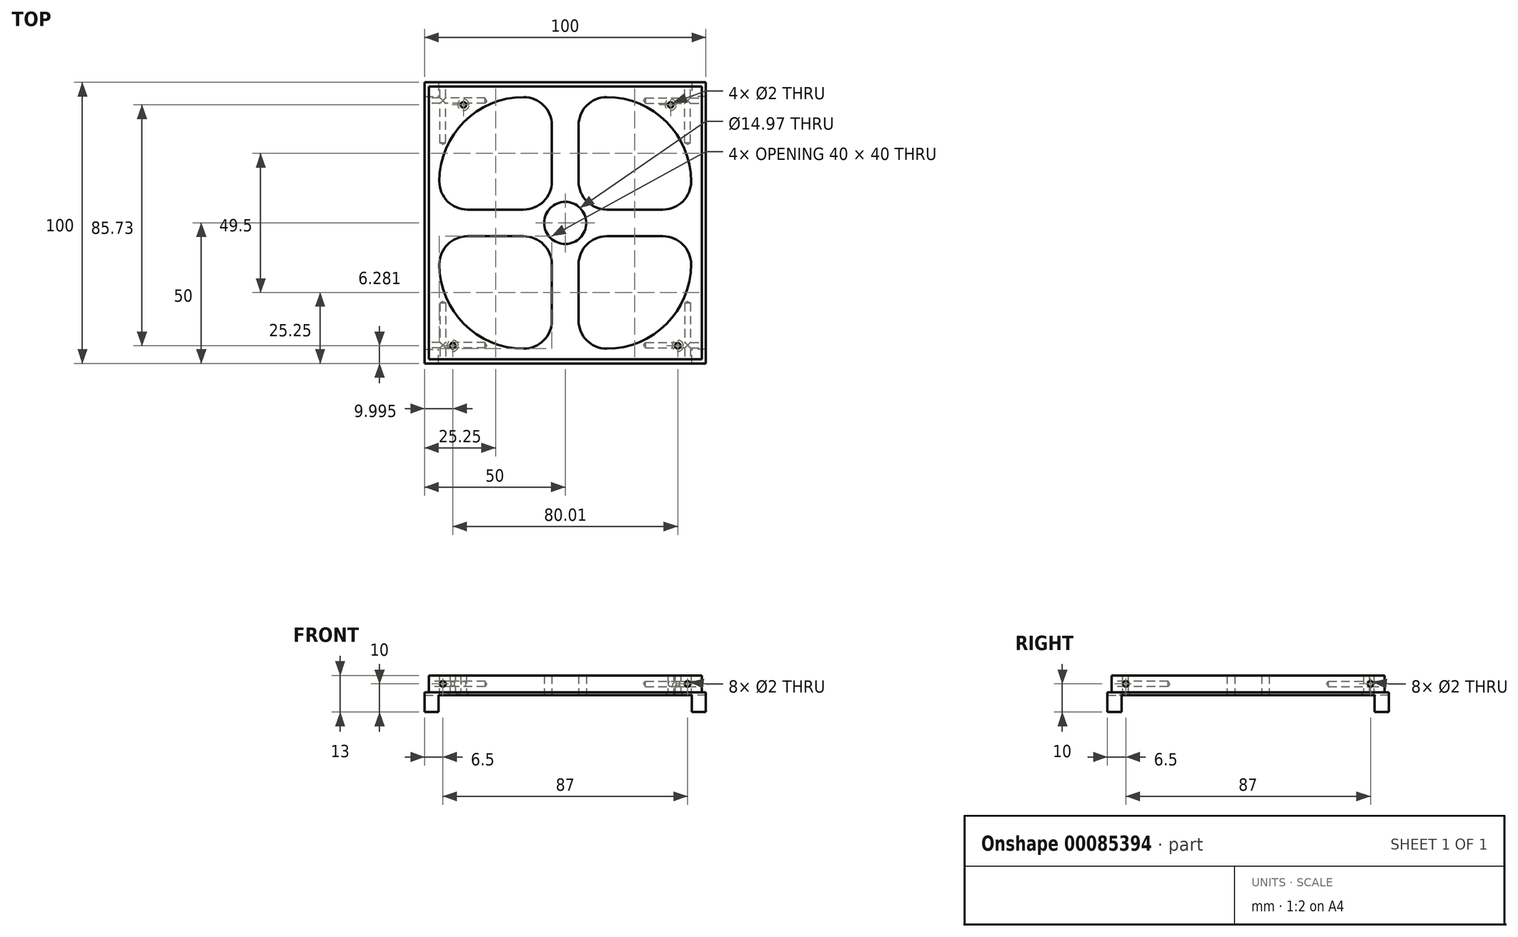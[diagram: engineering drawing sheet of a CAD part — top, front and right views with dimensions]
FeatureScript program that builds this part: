
annotation { "Feature Type Name" : "Feature", "Feature Type Description" : "" }
export const myFeature = defineFeature(function(context is Context, id is Id, definition is map)
    precondition{}
    {
        {
            var Q0;
            Q0=qCreatedBy(makeId("Top.planeOp"),FACE);
            var sketch = newSketch(context, id + "F0", { "sketchPlane" : qUnion([Q0])});
            skLineSegment(sketch, "E0.rect.bottom", {"start": v(-50, 50) * mm, "end": v(50, 50) * mm});
            skLineSegment(sketch, "E0.rect.top", {"start": v(-50, -50) * mm, "end": v(50, -50) * mm});
            skLineSegment(sketch, "E0.rect.left", {"start": v(-50, 50) * mm, "end": v(-50, -50) * mm});
            skLineSegment(sketch, "E0.rect.right", {"start": v(50, 50) * mm, "end": v(50, -50) * mm});
            skPoint(sketch, "E0.rect.middle", {"position": v(0, 0) * mm});
            skLineSegment(sketch, "E1.rect.bottom", {"start": v(-48.5, 48.5) * mm, "end": v(48.5, 48.5) * mm});
            skLineSegment(sketch, "E1.rect.top", {"start": v(-48.5, -48.5) * mm, "end": v(48.5, -48.5) * mm});
            skLineSegment(sketch, "E1.rect.left", {"start": v(-48.5, 48.5) * mm, "end": v(-48.5, -48.5) * mm});
            skLineSegment(sketch, "E1.rect.right", {"start": v(48.5, 48.5) * mm, "end": v(48.5, -48.5) * mm});
            skLineSegment(sketch, "E2.rect.bottom", {"start": v(-14.75, 4.75) * mm, "end": v(-34.75, 4.75) * mm});
            skLineSegment(sketch, "E2.rect.top", {"start": v(-14.75, 44.75) * mm, "end": v(-14.75, 44.75) * mm});
            skLineSegment(sketch, "E2.rect.left", {"start": v(-4.75, 14.75) * mm, "end": v(-4.75, 34.75) * mm});
            skLineSegment(sketch, "E2.rect.right", {"start": v(-44.75, 14.75) * mm, "end": v(-44.75, 14.75) * mm});
            skPoint(sketch, "E2.rect.middle", {"position": v(-24.75, 24.75) * mm});
            skPoint(sketch, "E3.visualSharp", {"position": v(-44.75, 44.75) * mm});
            skArc(sketch, "E3.filletArc", {"start": v(-14.75, 44.75) * mm, "mid": v(-35.96, 35.96) * mm, "end": v(-44.75, 14.75) * mm});
            skPoint(sketch, "E4.visualSharp", {"position": v(-4.75, 44.75) * mm});
            skArc(sketch, "E4.filletArc", {"start": v(-4.75, 34.75) * mm, "mid": v(-7.68, 41.82) * mm, "end": v(-14.75, 44.75) * mm});
            skPoint(sketch, "E5.visualSharp", {"position": v(-4.75, 4.75) * mm});
            skArc(sketch, "E5.filletArc", {"start": v(-14.75, 4.75) * mm, "mid": v(-7.68, 7.68) * mm, "end": v(-4.75, 14.75) * mm});
            skPoint(sketch, "E6.visualSharp", {"position": v(-44.75, 4.75) * mm});
            skArc(sketch, "E6.filletArc", {"start": v(-44.75, 14.75) * mm, "mid": v(-41.82, 7.68) * mm, "end": v(-34.75, 4.75) * mm});
            skLineSegment(sketch, "E7.MirrorCS", {"start": v(4.75, 14.75) * mm, "end": v(4.75, 34.75) * mm});
            skArc(sketch, "E8.MirrorCS", {"start": v(4.75, 34.75) * mm, "mid": v(7.68, 41.82) * mm, "end": v(14.75, 44.75) * mm});
            skLineSegment(sketch, "E9.MirrorCS", {"start": v(14.75, 44.75) * mm, "end": v(14.75, 44.75) * mm});
            skArc(sketch, "E10.MirrorCS", {"start": v(14.75, 44.75) * mm, "mid": v(35.96, 35.96) * mm, "end": v(44.75, 14.75) * mm});
            skLineSegment(sketch, "E11.MirrorCS", {"start": v(44.75, 14.75) * mm, "end": v(44.75, 14.75) * mm});
            skArc(sketch, "E12.MirrorCS", {"start": v(44.75, 14.75) * mm, "mid": v(41.82, 7.68) * mm, "end": v(34.75, 4.75) * mm});
            skLineSegment(sketch, "E13.MirrorCS", {"start": v(14.75, 4.75) * mm, "end": v(34.75, 4.75) * mm});
            skArc(sketch, "E14.MirrorCS", {"start": v(14.75, 4.75) * mm, "mid": v(7.68, 7.68) * mm, "end": v(4.75, 14.75) * mm});
            skPoint(sketch, "E15.MirrorP", {"position": v(24.75, 24.75) * mm});
            skArc(sketch, "E16.MirrorCS", {"start": v(14.75, -4.75) * mm, "mid": v(7.68, -7.68) * mm, "end": v(4.75, -14.75) * mm});
            skLineSegment(sketch, "E17.MirrorCS", {"start": v(4.75, -14.75) * mm, "end": v(4.75, -34.75) * mm});
            skArc(sketch, "E18.MirrorCS", {"start": v(4.75, -34.75) * mm, "mid": v(7.68, -41.82) * mm, "end": v(14.75, -44.75) * mm});
            skLineSegment(sketch, "E19.MirrorCS", {"start": v(14.75, -44.75) * mm, "end": v(14.75, -44.75) * mm});
            skArc(sketch, "E20.MirrorCS", {"start": v(14.75, -44.75) * mm, "mid": v(35.96, -35.96) * mm, "end": v(44.75, -14.75) * mm});
            skLineSegment(sketch, "E21.MirrorCS", {"start": v(44.75, -14.75) * mm, "end": v(44.75, -14.75) * mm});
            skArc(sketch, "E22.MirrorCS", {"start": v(44.75, -14.75) * mm, "mid": v(41.82, -7.68) * mm, "end": v(34.75, -4.75) * mm});
            skLineSegment(sketch, "E23.MirrorCS", {"start": v(14.75, -4.75) * mm, "end": v(34.75, -4.75) * mm});
            skPoint(sketch, "E24.MirrorP", {"position": v(24.75, -24.75) * mm});
            skLineSegment(sketch, "E25.MirrorCS", {"start": v(-4.75, -14.75) * mm, "end": v(-4.75, -34.75) * mm});
            skArc(sketch, "E26.MirrorCS", {"start": v(-14.75, -4.75) * mm, "mid": v(-7.68, -7.68) * mm, "end": v(-4.75, -14.75) * mm});
            skLineSegment(sketch, "E27.MirrorCS", {"start": v(-14.75, -4.75) * mm, "end": v(-34.75, -4.75) * mm});
            skArc(sketch, "E28.MirrorCS", {"start": v(-44.75, -14.75) * mm, "mid": v(-41.82, -7.68) * mm, "end": v(-34.75, -4.75) * mm});
            skLineSegment(sketch, "E29.MirrorCS", {"start": v(-44.75, -14.75) * mm, "end": v(-44.75, -14.75) * mm});
            skArc(sketch, "E30.MirrorCS", {"start": v(-14.75, -44.75) * mm, "mid": v(-35.96, -35.96) * mm, "end": v(-44.75, -14.75) * mm});
            skLineSegment(sketch, "E31.MirrorCS", {"start": v(-14.75, -44.75) * mm, "end": v(-14.75, -44.75) * mm});
            skArc(sketch, "E32.MirrorCS", {"start": v(-4.75, -34.75) * mm, "mid": v(-7.68, -41.82) * mm, "end": v(-14.75, -44.75) * mm});
            skPoint(sketch, "E33.MirrorP", {"position": v(-24.75, -24.75) * mm});
            skCircle(sketch, "E34", {"center": v(0, 0) * mm, "radius": 7.48 * mm});
            skPoint(sketch, "E35", {"position": v(-40, -42.87) * mm});
            skPoint(sketch, "E36", {"position": v(-48.5, 0) * mm});
            skPoint(sketch, "E37", {"position": v(48.5, 0) * mm});
            skLineSegment(sketch, "E38", {"start": v(-48.5, 0) * mm, "end": v(48.5, 0) * mm});
            skPoint(sketch, "E39.MirrorP", {"position": v(40, -42.87) * mm});
            skPoint(sketch, "E40", {"position": v(-36.2, 42.87) * mm});
            skPoint(sketch, "E41", {"position": v(37.47, 42.87) * mm});
            skSolve(sketch);
        }
        {
            var Q0;
            Q0=makeQuery(id+"F0.imprint","IMPRINT",FACE,{"disambiguationData":[TD([[makeQuery(id+"F0.imprint","IMPRINT",EDGE,{"derivedFrom":sQuery(id+"F0.wireOp",EDGE,"E1.rect.bottom")}),-1.0]])]});
            var Q1;
            {var subQ4=sQuery(id+"F0.wireOp",EDGE,"E1.rect.top");Q1=makeQuery(id+"F0.imprint","IMPRINT",FACE,{"disambiguationData":[TD([[makeQuery(id+"F0.imprint","IMPRINT",EDGE,{"derivedFrom":subQ4}),1.0]])]});}
            extrude(context, id + "F1", {"entities" : qUnion([Q0, Q1]), "depth" : 6 * mm});
        }
        {
            var Q0;
            Q0=qSketchRegion(id+"F0",true);
            var Q1;
            Q1=makeQuery(id+"F1.opExtrude","CAP_FACE",FACE,{"disambiguationData":[OSD([sQuery(id+"F0.wireOp",EDGE,"E1.rect.bottom"),sQuery(id+"F0.wireOp",EDGE,"E1.rect.top"),sQuery(id+"F0.wireOp",EDGE,"E1.rect.left"),sQuery(id+"F0.wireOp",EDGE,"E1.rect.right"),sQuery(id+"F0.wireOp",EDGE,"E2.rect.bottom"),sQuery(id+"F0.wireOp",EDGE,"E2.rect.top"),sQuery(id+"F0.wireOp",EDGE,"E2.rect.left"),sQuery(id+"F0.wireOp",EDGE,"E2.rect.right"),sQuery(id+"F0.wireOp",EDGE,"d764ca65-7f6a-4e13-98eb-a7907a3d072d0.MirrorCS"),sQuery(id+"F0.wireOp",EDGE,"4e8c5bec-c53d-4312-8259-349e49f543fe0.MirrorCS"),sQuery(id+"F0.wireOp",EDGE,"d6a0bf7c-e4bc-484e-b3d5-183d898144500.MirrorCS"),sQuery(id+"F0.wireOp",EDGE,"45a758ec-378c-46c5-b086-a70cc1cacffd0.MirrorCS"),sQuery(id+"F0.wireOp",EDGE,"a64d5360-d78c-41ef-9f44-8c8436a09bba0.MirrorCS"),sQuery(id+"F0.wireOp",EDGE,"c998a958-b69a-464e-a296-dd7f6d349ec80.MirrorCS"),sQuery(id+"F0.wireOp",EDGE,"a4bf1b2a-a2f4-4ab3-9d73-85797b196d270.MirrorCS"),sQuery(id+"F0.wireOp",EDGE,"ecd2f3fb-4ea3-4913-80f4-94ebebe2d04e0.MirrorCS"),sQuery(id+"F0.wireOp",EDGE,"085a2cb5-2e3f-4cc3-a5b9-01c6e75669f10.MirrorCS"),sQuery(id+"F0.wireOp",EDGE,"73d67a52-dadc-4bd6-8141-d25047cb753b0.MirrorCS"),sQuery(id+"F0.wireOp",EDGE,"8f6832c0-858d-4205-8574-29f35786d1620.MirrorCS"),sQuery(id+"F0.wireOp",EDGE,"ecc9a695-4792-4055-9804-abf58933c5b20.MirrorCS")])],"isStart":false});
            extrude(context, id + "F2", {"entities" : qUnion([Q0, Q1]), "operationType" : NewBodyOperationType.ADD, "depth" : 1 * mm});
        }
        {
            var Q0;
            {var subQ0=sQuery(id+"F0.wireOp",EDGE,"E1.rect.bottom");Q0=makeQuery(id+"F2.boolean.opBoolean","MERGE",FACE,{"derivedFrom":[makeQuery(id+"F1.opExtrude","SWEPT_FACE",FACE,{"disambiguationData":[OSD([subQ0])]}),makeQuery(id+"F2.opExtrude","SWEPT_FACE",FACE,{"disambiguationData":[OSD([subQ0]),TDD([makeQuery(id+"F1.opExtrude","CAP_EDGE",EDGE,{"disambiguationData":[OSD([subQ0])],"isStart":false})])]})]});}
            var sketch = newSketch(context, id + "F3", { "sketchPlane" : qUnion([Q0])});
            skPoint(sketch, "E42", {"position": v(-43.5, 4) * mm});
            skPoint(sketch, "E43.MirrorP", {"position": v(43.5, 4) * mm});
            skSolve(sketch);
        }
        {
            var Q0;
            Q0=sQuery(id+"F3.wireOp",VERTEX,"E42");
            var Q1;
            Q1=sQuery(id+"F3.wireOp",VERTEX,"E43.MirrorP");
            var Q2;
            Q2=makeQuery(id+"F1.opExtrude","SWEPT_BODY",BODY,{"disambiguationData":[OSD([sQuery(id+"F0.wireOp",EDGE,"E1.rect.bottom"),sQuery(id+"F0.wireOp",EDGE,"E1.rect.top"),sQuery(id+"F0.wireOp",EDGE,"E1.rect.left"),sQuery(id+"F0.wireOp",EDGE,"E1.rect.right"),sQuery(id+"F0.wireOp",EDGE,"E2.rect.bottom"),sQuery(id+"F0.wireOp",EDGE,"E2.rect.top"),sQuery(id+"F0.wireOp",EDGE,"E2.rect.left"),sQuery(id+"F0.wireOp",EDGE,"E2.rect.right"),sQuery(id+"F0.wireOp",EDGE,"E3.filletArc"),sQuery(id+"F0.wireOp",EDGE,"E4.filletArc"),sQuery(id+"F0.wireOp",EDGE,"E5.filletArc"),sQuery(id+"F0.wireOp",EDGE,"E6.filletArc"),sQuery(id+"F0.wireOp",EDGE,"E7.MirrorCS"),sQuery(id+"F0.wireOp",EDGE,"E8.MirrorCS"),sQuery(id+"F0.wireOp",EDGE,"E9.MirrorCS"),sQuery(id+"F0.wireOp",EDGE,"E10.MirrorCS"),sQuery(id+"F0.wireOp",EDGE,"E11.MirrorCS"),sQuery(id+"F0.wireOp",EDGE,"E12.MirrorCS"),sQuery(id+"F0.wireOp",EDGE,"E13.MirrorCS"),sQuery(id+"F0.wireOp",EDGE,"E14.MirrorCS"),sQuery(id+"F0.wireOp",EDGE,"E16.MirrorCS"),sQuery(id+"F0.wireOp",EDGE,"E17.MirrorCS"),sQuery(id+"F0.wireOp",EDGE,"E18.MirrorCS"),sQuery(id+"F0.wireOp",EDGE,"E19.MirrorCS"),sQuery(id+"F0.wireOp",EDGE,"E20.MirrorCS"),sQuery(id+"F0.wireOp",EDGE,"E21.MirrorCS"),sQuery(id+"F0.wireOp",EDGE,"E22.MirrorCS"),sQuery(id+"F0.wireOp",EDGE,"E23.MirrorCS"),sQuery(id+"F0.wireOp",EDGE,"E25.MirrorCS"),sQuery(id+"F0.wireOp",EDGE,"E26.MirrorCS"),sQuery(id+"F0.wireOp",EDGE,"E27.MirrorCS"),sQuery(id+"F0.wireOp",EDGE,"E28.MirrorCS"),sQuery(id+"F0.wireOp",EDGE,"E29.MirrorCS"),sQuery(id+"F0.wireOp",EDGE,"E30.MirrorCS"),sQuery(id+"F0.wireOp",EDGE,"E31.MirrorCS"),sQuery(id+"F0.wireOp",EDGE,"E32.MirrorCS")])]});
            hole(context, id + "F4", {"style" : HoleStyle.SIMPLE, "holeDiameter" : 2 * mm, "endStyle" : HoleEndStyle.BLIND, "holeDepth" : 20 * mm, "locations" : qUnion([Q0, Q1]), "scope" : qUnion([Q2])});
        }
        {
            var Q0;
            {var subQ0=sQuery(id+"F0.wireOp",EDGE,"E1.rect.left");Q0=makeQuery(id+"F2.boolean.opBoolean","MERGE",FACE,{"derivedFrom":[makeQuery(id+"F1.opExtrude","SWEPT_FACE",FACE,{"disambiguationData":[OSD([subQ0])]}),makeQuery(id+"F2.opExtrude","SWEPT_FACE",FACE,{"disambiguationData":[OSD([subQ0]),TDD([makeQuery(id+"F1.opExtrude","CAP_EDGE",EDGE,{"disambiguationData":[OSD([subQ0])],"isStart":false})])]})]});}
            var sketch = newSketch(context, id + "F5", { "sketchPlane" : qUnion([Q0])});
            skPoint(sketch, "E44", {"position": v(-43.5, 4) * mm});
            skPoint(sketch, "E45.MirrorP", {"position": v(43.5, 4) * mm});
            skSolve(sketch);
        }
        {
            var Q0;
            Q0=sQuery(id+"F5.wireOp",VERTEX,"E44");
            var Q1;
            Q1=sQuery(id+"F5.wireOp",VERTEX,"E45.MirrorP");
            var Q2;
            Q2=makeQuery(id+"F1.opExtrude","SWEPT_BODY",BODY,{"disambiguationData":[OSD([sQuery(id+"F0.wireOp",EDGE,"E1.rect.bottom"),sQuery(id+"F0.wireOp",EDGE,"E1.rect.top"),sQuery(id+"F0.wireOp",EDGE,"E1.rect.left"),sQuery(id+"F0.wireOp",EDGE,"E1.rect.right"),sQuery(id+"F0.wireOp",EDGE,"E2.rect.bottom"),sQuery(id+"F0.wireOp",EDGE,"E2.rect.top"),sQuery(id+"F0.wireOp",EDGE,"E2.rect.left"),sQuery(id+"F0.wireOp",EDGE,"E2.rect.right"),sQuery(id+"F0.wireOp",EDGE,"E3.filletArc"),sQuery(id+"F0.wireOp",EDGE,"E4.filletArc"),sQuery(id+"F0.wireOp",EDGE,"E5.filletArc"),sQuery(id+"F0.wireOp",EDGE,"E6.filletArc"),sQuery(id+"F0.wireOp",EDGE,"E7.MirrorCS"),sQuery(id+"F0.wireOp",EDGE,"E8.MirrorCS"),sQuery(id+"F0.wireOp",EDGE,"E9.MirrorCS"),sQuery(id+"F0.wireOp",EDGE,"E10.MirrorCS"),sQuery(id+"F0.wireOp",EDGE,"E11.MirrorCS"),sQuery(id+"F0.wireOp",EDGE,"E12.MirrorCS"),sQuery(id+"F0.wireOp",EDGE,"E13.MirrorCS"),sQuery(id+"F0.wireOp",EDGE,"E14.MirrorCS"),sQuery(id+"F0.wireOp",EDGE,"E16.MirrorCS"),sQuery(id+"F0.wireOp",EDGE,"E17.MirrorCS"),sQuery(id+"F0.wireOp",EDGE,"E18.MirrorCS"),sQuery(id+"F0.wireOp",EDGE,"E19.MirrorCS"),sQuery(id+"F0.wireOp",EDGE,"E20.MirrorCS"),sQuery(id+"F0.wireOp",EDGE,"E21.MirrorCS"),sQuery(id+"F0.wireOp",EDGE,"E22.MirrorCS"),sQuery(id+"F0.wireOp",EDGE,"E23.MirrorCS"),sQuery(id+"F0.wireOp",EDGE,"E25.MirrorCS"),sQuery(id+"F0.wireOp",EDGE,"E26.MirrorCS"),sQuery(id+"F0.wireOp",EDGE,"E27.MirrorCS"),sQuery(id+"F0.wireOp",EDGE,"E28.MirrorCS"),sQuery(id+"F0.wireOp",EDGE,"E29.MirrorCS"),sQuery(id+"F0.wireOp",EDGE,"E30.MirrorCS"),sQuery(id+"F0.wireOp",EDGE,"E31.MirrorCS"),sQuery(id+"F0.wireOp",EDGE,"E32.MirrorCS")])]});
            hole(context, id + "F6", {"style" : HoleStyle.SIMPLE, "holeDiameter" : 2 * mm, "endStyle" : HoleEndStyle.BLIND, "holeDepth" : 20 * mm, "locations" : qUnion([Q0, Q1]), "scope" : qUnion([Q2])});
        }
        {
            var Q0;
            {var subQ0=sQuery(id+"F0.wireOp",EDGE,"E1.rect.top");Q0=makeQuery(id+"F2.boolean.opBoolean","MERGE",FACE,{"derivedFrom":[makeQuery(id+"F1.opExtrude","SWEPT_FACE",FACE,{"disambiguationData":[OSD([subQ0])]}),makeQuery(id+"F2.opExtrude","SWEPT_FACE",FACE,{"disambiguationData":[OSD([subQ0]),TDD([makeQuery(id+"F1.opExtrude","CAP_EDGE",EDGE,{"disambiguationData":[OSD([subQ0])],"isStart":false})])]})]});}
            var sketch = newSketch(context, id + "F7", { "sketchPlane" : qUnion([Q0])});
            skPoint(sketch, "E46", {"position": v(-43.5, 4) * mm});
            skPoint(sketch, "E47.MirrorP", {"position": v(43.5, 4) * mm});
            skSolve(sketch);
        }
        {
            var Q0;
            Q0=sQuery(id+"F7.wireOp",VERTEX,"E46");
            var Q1;
            Q1=sQuery(id+"F7.wireOp",VERTEX,"E47.MirrorP");
            var Q2;
            Q2=makeQuery(id+"F1.opExtrude","SWEPT_BODY",BODY,{"disambiguationData":[OSD([sQuery(id+"F0.wireOp",EDGE,"E1.rect.bottom"),sQuery(id+"F0.wireOp",EDGE,"E1.rect.top"),sQuery(id+"F0.wireOp",EDGE,"E1.rect.left"),sQuery(id+"F0.wireOp",EDGE,"E1.rect.right"),sQuery(id+"F0.wireOp",EDGE,"E2.rect.bottom"),sQuery(id+"F0.wireOp",EDGE,"E2.rect.top"),sQuery(id+"F0.wireOp",EDGE,"E2.rect.left"),sQuery(id+"F0.wireOp",EDGE,"E2.rect.right"),sQuery(id+"F0.wireOp",EDGE,"E3.filletArc"),sQuery(id+"F0.wireOp",EDGE,"E4.filletArc"),sQuery(id+"F0.wireOp",EDGE,"E5.filletArc"),sQuery(id+"F0.wireOp",EDGE,"E6.filletArc"),sQuery(id+"F0.wireOp",EDGE,"E7.MirrorCS"),sQuery(id+"F0.wireOp",EDGE,"E8.MirrorCS"),sQuery(id+"F0.wireOp",EDGE,"E9.MirrorCS"),sQuery(id+"F0.wireOp",EDGE,"E10.MirrorCS"),sQuery(id+"F0.wireOp",EDGE,"E11.MirrorCS"),sQuery(id+"F0.wireOp",EDGE,"E12.MirrorCS"),sQuery(id+"F0.wireOp",EDGE,"E13.MirrorCS"),sQuery(id+"F0.wireOp",EDGE,"E14.MirrorCS"),sQuery(id+"F0.wireOp",EDGE,"E16.MirrorCS"),sQuery(id+"F0.wireOp",EDGE,"E17.MirrorCS"),sQuery(id+"F0.wireOp",EDGE,"E18.MirrorCS"),sQuery(id+"F0.wireOp",EDGE,"E19.MirrorCS"),sQuery(id+"F0.wireOp",EDGE,"E20.MirrorCS"),sQuery(id+"F0.wireOp",EDGE,"E21.MirrorCS"),sQuery(id+"F0.wireOp",EDGE,"E22.MirrorCS"),sQuery(id+"F0.wireOp",EDGE,"E23.MirrorCS"),sQuery(id+"F0.wireOp",EDGE,"E25.MirrorCS"),sQuery(id+"F0.wireOp",EDGE,"E26.MirrorCS"),sQuery(id+"F0.wireOp",EDGE,"E27.MirrorCS"),sQuery(id+"F0.wireOp",EDGE,"E28.MirrorCS"),sQuery(id+"F0.wireOp",EDGE,"E29.MirrorCS"),sQuery(id+"F0.wireOp",EDGE,"E30.MirrorCS"),sQuery(id+"F0.wireOp",EDGE,"E31.MirrorCS"),sQuery(id+"F0.wireOp",EDGE,"E32.MirrorCS")])]});
            hole(context, id + "F8", {"style" : HoleStyle.SIMPLE, "holeDiameter" : 2 * mm, "endStyle" : HoleEndStyle.BLIND, "holeDepth" : 20 * mm, "locations" : qUnion([Q0, Q1]), "scope" : qUnion([Q2])});
        }
        {
            var Q0;
            {var subQ0=sQuery(id+"F0.wireOp",EDGE,"E1.rect.right");Q0=makeQuery(id+"F2.boolean.opBoolean","MERGE",FACE,{"derivedFrom":[makeQuery(id+"F1.opExtrude","SWEPT_FACE",FACE,{"disambiguationData":[OSD([subQ0])]}),makeQuery(id+"F2.opExtrude","SWEPT_FACE",FACE,{"disambiguationData":[OSD([subQ0]),TDD([makeQuery(id+"F1.opExtrude","CAP_EDGE",EDGE,{"disambiguationData":[OSD([subQ0])],"isStart":false})])]})]});}
            var sketch = newSketch(context, id + "F9", { "sketchPlane" : qUnion([Q0])});
            skPoint(sketch, "E48", {"position": v(-43.5, 4) * mm});
            skPoint(sketch, "E49.MirrorP", {"position": v(43.5, 4) * mm});
            skSolve(sketch);
        }
        {
            var Q0;
            Q0=sQuery(id+"F9.wireOp",VERTEX,"E48");
            var Q1;
            Q1=sQuery(id+"F9.wireOp",VERTEX,"E49.MirrorP");
            var Q2;
            Q2=makeQuery(id+"F1.opExtrude","SWEPT_BODY",BODY,{"disambiguationData":[OSD([sQuery(id+"F0.wireOp",EDGE,"E1.rect.bottom"),sQuery(id+"F0.wireOp",EDGE,"E1.rect.top"),sQuery(id+"F0.wireOp",EDGE,"E1.rect.left"),sQuery(id+"F0.wireOp",EDGE,"E1.rect.right"),sQuery(id+"F0.wireOp",EDGE,"E2.rect.bottom"),sQuery(id+"F0.wireOp",EDGE,"E2.rect.top"),sQuery(id+"F0.wireOp",EDGE,"E2.rect.left"),sQuery(id+"F0.wireOp",EDGE,"E2.rect.right"),sQuery(id+"F0.wireOp",EDGE,"E3.filletArc"),sQuery(id+"F0.wireOp",EDGE,"E4.filletArc"),sQuery(id+"F0.wireOp",EDGE,"E5.filletArc"),sQuery(id+"F0.wireOp",EDGE,"E6.filletArc"),sQuery(id+"F0.wireOp",EDGE,"E7.MirrorCS"),sQuery(id+"F0.wireOp",EDGE,"E8.MirrorCS"),sQuery(id+"F0.wireOp",EDGE,"E9.MirrorCS"),sQuery(id+"F0.wireOp",EDGE,"E10.MirrorCS"),sQuery(id+"F0.wireOp",EDGE,"E11.MirrorCS"),sQuery(id+"F0.wireOp",EDGE,"E12.MirrorCS"),sQuery(id+"F0.wireOp",EDGE,"E13.MirrorCS"),sQuery(id+"F0.wireOp",EDGE,"E14.MirrorCS"),sQuery(id+"F0.wireOp",EDGE,"E16.MirrorCS"),sQuery(id+"F0.wireOp",EDGE,"E17.MirrorCS"),sQuery(id+"F0.wireOp",EDGE,"E18.MirrorCS"),sQuery(id+"F0.wireOp",EDGE,"E19.MirrorCS"),sQuery(id+"F0.wireOp",EDGE,"E20.MirrorCS"),sQuery(id+"F0.wireOp",EDGE,"E21.MirrorCS"),sQuery(id+"F0.wireOp",EDGE,"E22.MirrorCS"),sQuery(id+"F0.wireOp",EDGE,"E23.MirrorCS"),sQuery(id+"F0.wireOp",EDGE,"E25.MirrorCS"),sQuery(id+"F0.wireOp",EDGE,"E26.MirrorCS"),sQuery(id+"F0.wireOp",EDGE,"E27.MirrorCS"),sQuery(id+"F0.wireOp",EDGE,"E28.MirrorCS"),sQuery(id+"F0.wireOp",EDGE,"E29.MirrorCS"),sQuery(id+"F0.wireOp",EDGE,"E30.MirrorCS"),sQuery(id+"F0.wireOp",EDGE,"E31.MirrorCS"),sQuery(id+"F0.wireOp",EDGE,"E32.MirrorCS")])]});
            hole(context, id + "F10", {"style" : HoleStyle.SIMPLE, "holeDiameter" : 2 * mm, "endStyle" : HoleEndStyle.BLIND, "holeDepth" : 20 * mm, "locations" : qUnion([Q0, Q1]), "scope" : qUnion([Q2])});
        }
        {
            var Q0;
            {var subQ0=sQuery(id+"F0.wireOp",EDGE,"E1.rect.bottom");var subQ1=sQuery(id+"F0.wireOp",EDGE,"E1.rect.top");var subQ2=sQuery(id+"F0.wireOp",EDGE,"E1.rect.left");var subQ3=sQuery(id+"F0.wireOp",EDGE,"E1.rect.right");Q0=makeQuery(id+"F2.boolean.opBoolean","MERGE",FACE,{"derivedFrom":[makeQuery(id+"F1.opExtrude","CAP_FACE",FACE,{"disambiguationData":[OSD([subQ0,subQ1,subQ2,subQ3,sQuery(id+"F0.wireOp",EDGE,"E2.rect.bottom"),sQuery(id+"F0.wireOp",EDGE,"E2.rect.top"),sQuery(id+"F0.wireOp",EDGE,"E2.rect.left"),sQuery(id+"F0.wireOp",EDGE,"E2.rect.right"),sQuery(id+"F0.wireOp",EDGE,"E3.filletArc"),sQuery(id+"F0.wireOp",EDGE,"E4.filletArc"),sQuery(id+"F0.wireOp",EDGE,"E5.filletArc"),sQuery(id+"F0.wireOp",EDGE,"E6.filletArc"),sQuery(id+"F0.wireOp",EDGE,"E7.MirrorCS"),sQuery(id+"F0.wireOp",EDGE,"E8.MirrorCS"),sQuery(id+"F0.wireOp",EDGE,"E9.MirrorCS"),sQuery(id+"F0.wireOp",EDGE,"E10.MirrorCS"),sQuery(id+"F0.wireOp",EDGE,"E11.MirrorCS"),sQuery(id+"F0.wireOp",EDGE,"E12.MirrorCS"),sQuery(id+"F0.wireOp",EDGE,"E13.MirrorCS"),sQuery(id+"F0.wireOp",EDGE,"E14.MirrorCS"),sQuery(id+"F0.wireOp",EDGE,"E16.MirrorCS"),sQuery(id+"F0.wireOp",EDGE,"E17.MirrorCS"),sQuery(id+"F0.wireOp",EDGE,"E18.MirrorCS"),sQuery(id+"F0.wireOp",EDGE,"E19.MirrorCS"),sQuery(id+"F0.wireOp",EDGE,"E20.MirrorCS"),sQuery(id+"F0.wireOp",EDGE,"E21.MirrorCS"),sQuery(id+"F0.wireOp",EDGE,"E22.MirrorCS"),sQuery(id+"F0.wireOp",EDGE,"E23.MirrorCS"),sQuery(id+"F0.wireOp",EDGE,"E25.MirrorCS"),sQuery(id+"F0.wireOp",EDGE,"E26.MirrorCS"),sQuery(id+"F0.wireOp",EDGE,"E27.MirrorCS"),sQuery(id+"F0.wireOp",EDGE,"E28.MirrorCS"),sQuery(id+"F0.wireOp",EDGE,"E29.MirrorCS"),sQuery(id+"F0.wireOp",EDGE,"E30.MirrorCS"),sQuery(id+"F0.wireOp",EDGE,"E31.MirrorCS"),sQuery(id+"F0.wireOp",EDGE,"E32.MirrorCS")])],"isStart":true}),makeQuery(id+"F2.opExtrude","CAP_FACE",FACE,{"disambiguationData":[OSD([sQuery(id+"F0.wireOp",EDGE,"E0.rect.bottom"),sQuery(id+"F0.wireOp",EDGE,"E0.rect.top"),sQuery(id+"F0.wireOp",EDGE,"E0.rect.left"),sQuery(id+"F0.wireOp",EDGE,"E0.rect.right"),subQ0,subQ1,subQ2,subQ3])],"isStart":true})]});}
            var sketch = newSketch(context, id + "F11", { "sketchPlane" : qUnion([Q0])});
            skPoint(sketch, "E50", {"position": v(-36.2, -42.01) * mm});
            skPoint(sketch, "E51", {"position": v(40, 43.72) * mm});
            skPoint(sketch, "E52", {"position": v(37.47, -42.01) * mm});
            skPoint(sketch, "E53", {"position": v(-40, 43.72) * mm});
            skLineSegment(sketch, "E54.bottom", {"start": v(50, -50) * mm, "end": v(45, -50) * mm});
            skLineSegment(sketch, "E54.top", {"start": v(50, -45) * mm, "end": v(45, -45) * mm});
            skLineSegment(sketch, "E54.left", {"start": v(50, -50) * mm, "end": v(50, -45) * mm});
            skLineSegment(sketch, "E54.right", {"start": v(45, -50) * mm, "end": v(45, -45) * mm});
            skLineSegment(sketch, "E55.MirrorCS", {"start": v(-50, -50) * mm, "end": v(-50, -45) * mm});
            skLineSegment(sketch, "E56.MirrorCS", {"start": v(-45, -50) * mm, "end": v(-45, -45) * mm});
            skLineSegment(sketch, "E57.MirrorCS", {"start": v(-50, -45) * mm, "end": v(-45, -45) * mm});
            skLineSegment(sketch, "E58.MirrorCS", {"start": v(-50, -50) * mm, "end": v(-45, -50) * mm});
            skLineSegment(sketch, "E59.MirrorCS", {"start": v(-50, 50) * mm, "end": v(-45, 50) * mm});
            skLineSegment(sketch, "E60.MirrorCS", {"start": v(-50, 45) * mm, "end": v(-45, 45) * mm});
            skLineSegment(sketch, "E61.MirrorCS", {"start": v(-50, 50) * mm, "end": v(-50, 45) * mm});
            skLineSegment(sketch, "E62.MirrorCS", {"start": v(-45, 50) * mm, "end": v(-45, 45) * mm});
            skLineSegment(sketch, "E63.MirrorCS", {"start": v(50, 50) * mm, "end": v(45, 50) * mm});
            skLineSegment(sketch, "E64.MirrorCS", {"start": v(50, 45) * mm, "end": v(45, 45) * mm});
            skLineSegment(sketch, "E65.MirrorCS", {"start": v(50, 50) * mm, "end": v(50, 45) * mm});
            skLineSegment(sketch, "E66.MirrorCS", {"start": v(45, 50) * mm, "end": v(45, 45) * mm});
            skSolve(sketch);
        }
        {
            var Q0;
            Q0=sQuery(id+"F11.wireOp",VERTEX,"E50");
            var Q1;
            Q1=sQuery(id+"F11.wireOp",VERTEX,"E53");
            var Q2;
            Q2=sQuery(id+"F11.wireOp",VERTEX,"E51");
            var Q3;
            Q3=sQuery(id+"F11.wireOp",VERTEX,"E52");
            var Q4;
            Q4=makeQuery(id+"F1.opExtrude","SWEPT_BODY",BODY,{"disambiguationData":[OSD([sQuery(id+"F0.wireOp",EDGE,"E1.rect.bottom"),sQuery(id+"F0.wireOp",EDGE,"E1.rect.top"),sQuery(id+"F0.wireOp",EDGE,"E1.rect.left"),sQuery(id+"F0.wireOp",EDGE,"E1.rect.right"),sQuery(id+"F0.wireOp",EDGE,"E2.rect.bottom"),sQuery(id+"F0.wireOp",EDGE,"E2.rect.top"),sQuery(id+"F0.wireOp",EDGE,"E2.rect.left"),sQuery(id+"F0.wireOp",EDGE,"E2.rect.right"),sQuery(id+"F0.wireOp",EDGE,"E3.filletArc"),sQuery(id+"F0.wireOp",EDGE,"E4.filletArc"),sQuery(id+"F0.wireOp",EDGE,"E5.filletArc"),sQuery(id+"F0.wireOp",EDGE,"E6.filletArc"),sQuery(id+"F0.wireOp",EDGE,"E7.MirrorCS"),sQuery(id+"F0.wireOp",EDGE,"E8.MirrorCS"),sQuery(id+"F0.wireOp",EDGE,"E9.MirrorCS"),sQuery(id+"F0.wireOp",EDGE,"E10.MirrorCS"),sQuery(id+"F0.wireOp",EDGE,"E11.MirrorCS"),sQuery(id+"F0.wireOp",EDGE,"E12.MirrorCS"),sQuery(id+"F0.wireOp",EDGE,"E13.MirrorCS"),sQuery(id+"F0.wireOp",EDGE,"E14.MirrorCS"),sQuery(id+"F0.wireOp",EDGE,"E16.MirrorCS"),sQuery(id+"F0.wireOp",EDGE,"E17.MirrorCS"),sQuery(id+"F0.wireOp",EDGE,"E18.MirrorCS"),sQuery(id+"F0.wireOp",EDGE,"E19.MirrorCS"),sQuery(id+"F0.wireOp",EDGE,"E20.MirrorCS"),sQuery(id+"F0.wireOp",EDGE,"E21.MirrorCS"),sQuery(id+"F0.wireOp",EDGE,"E22.MirrorCS"),sQuery(id+"F0.wireOp",EDGE,"E23.MirrorCS"),sQuery(id+"F0.wireOp",EDGE,"E25.MirrorCS"),sQuery(id+"F0.wireOp",EDGE,"E26.MirrorCS"),sQuery(id+"F0.wireOp",EDGE,"E27.MirrorCS"),sQuery(id+"F0.wireOp",EDGE,"E28.MirrorCS"),sQuery(id+"F0.wireOp",EDGE,"E29.MirrorCS"),sQuery(id+"F0.wireOp",EDGE,"E30.MirrorCS"),sQuery(id+"F0.wireOp",EDGE,"E31.MirrorCS"),sQuery(id+"F0.wireOp",EDGE,"E32.MirrorCS")])]});
            hole(context, id + "F12", {"style" : HoleStyle.C_SINK, "holeDiameter" : 2 * mm, "cSinkDiameter" : 4 * mm, "endStyle" : HoleEndStyle.THROUGH, "locations" : qUnion([Q0, Q1, Q2, Q3]), "scope" : qUnion([Q4]), "cSinkAngle" : 90 * degree});
        }
        {
            var Q0;
            Q0=makeQuery(id+"F11.imprint","IMPRINT",FACE,{"disambiguationData":[TD([[makeQuery(id+"F11.imprint","IMPRINT",EDGE,{"derivedFrom":sQuery(id+"F11.wireOp",EDGE,"E59.MirrorCS")}),-1.0]])]});
            var Q1;
            Q1=makeQuery(id+"F11.imprint","IMPRINT",FACE,{"disambiguationData":[TD([[makeQuery(id+"F11.imprint","IMPRINT",EDGE,{"derivedFrom":sQuery(id+"F11.wireOp",EDGE,"E63.MirrorCS")}),-1.0]])]});
            var Q2;
            Q2=makeQuery(id+"F11.imprint","IMPRINT",FACE,{"disambiguationData":[TD([[makeQuery(id+"F11.imprint","IMPRINT",EDGE,{"derivedFrom":sQuery(id+"F11.wireOp",EDGE,"E54.bottom")}),1.0]])]});
            var Q3;
            Q3=makeQuery(id+"F11.imprint","IMPRINT",FACE,{"disambiguationData":[TD([[makeQuery(id+"F11.imprint","IMPRINT",EDGE,{"derivedFrom":sQuery(id+"F11.wireOp",EDGE,"E55.MirrorCS")}),-1.0]])]});
            extrude(context, id + "F13", {"entities" : qUnion([Q0, Q1, Q2, Q3]), "operationType" : NewBodyOperationType.ADD, "depth" : 6 * mm});
        }
    });
